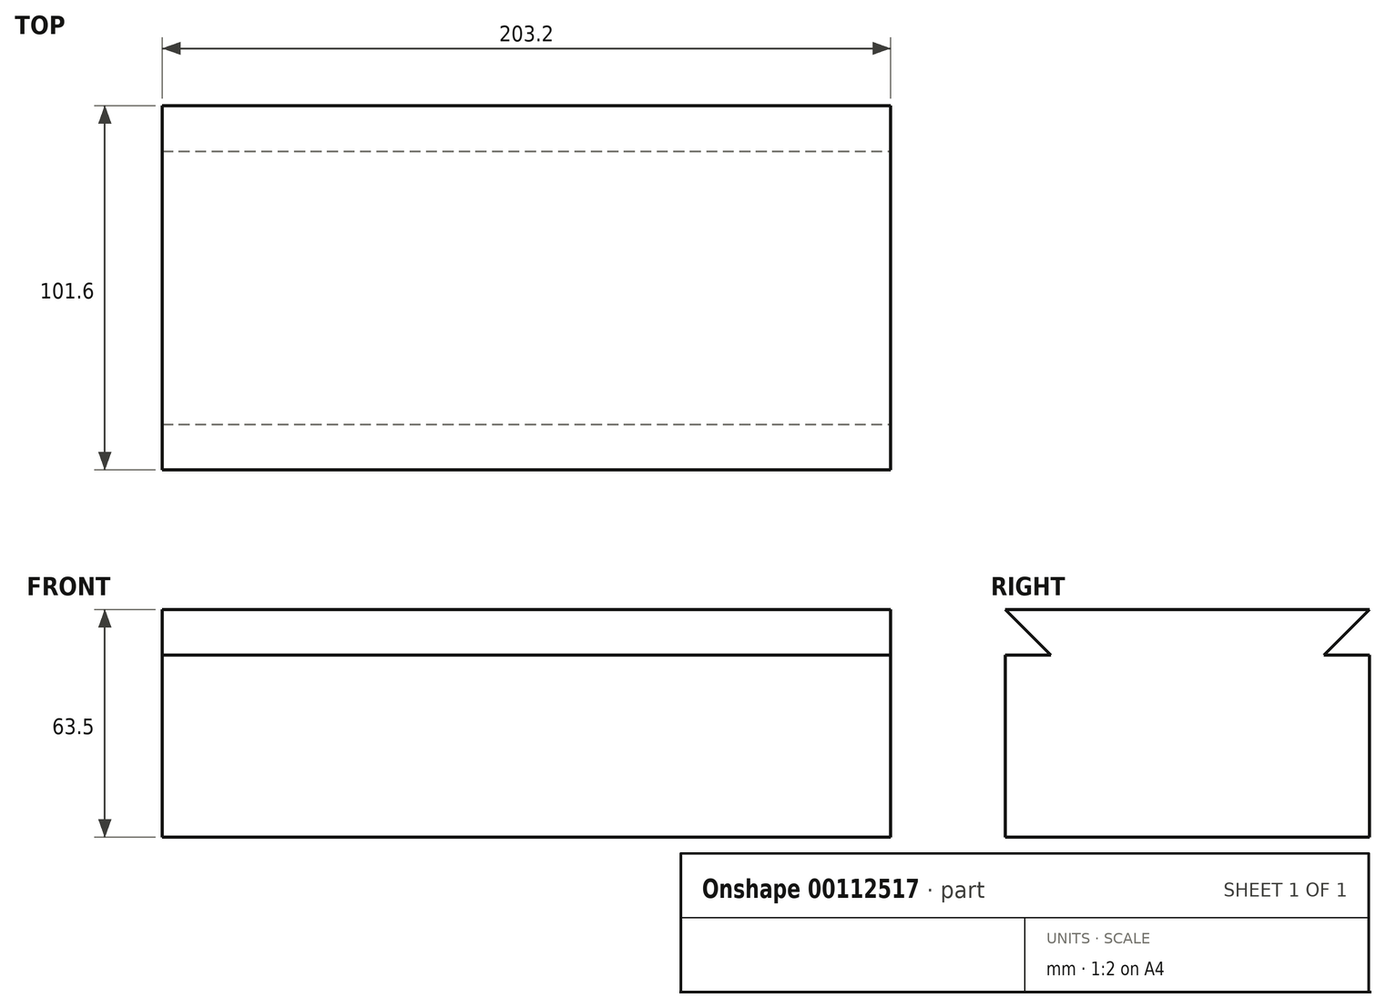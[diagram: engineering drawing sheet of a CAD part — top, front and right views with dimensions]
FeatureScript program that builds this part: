
annotation { "Feature Type Name" : "Feature", "Feature Type Description" : "" }
export const myFeature = defineFeature(function(context is Context, id is Id, definition is map)
    precondition{}
    {
        {
            var Q0;
            Q0=qCreatedBy(makeId("Top.planeOp"),FACE);
            var sketch = newSketch(context, id + "F0", { "sketchPlane" : qUnion([Q0])});
            skLineSegment(sketch, "E0.bottom", {"start": v(101.6, -50.8) * mm, "end": v(-101.6, -50.8) * mm});
            skLineSegment(sketch, "E0.top", {"start": v(101.6, 50.8) * mm, "end": v(-101.6, 50.8) * mm});
            skLineSegment(sketch, "E0.left", {"start": v(101.6, -50.8) * mm, "end": v(101.6, 50.8) * mm});
            skLineSegment(sketch, "E0.right", {"start": v(-101.6, -50.8) * mm, "end": v(-101.6, 50.8) * mm});
            skPoint(sketch, "E0.middle", {"position": v(0, 0) * mm});
            skSolve(sketch);
        }
        {
            var Q0;
            Q0=makeQuery(id+"F0.imprint","IMPRINT",FACE,{"disambiguationData":[TD([[makeQuery(id+"F0.imprint","IMPRINT",EDGE,{"derivedFrom":sQuery(id+"F0.wireOp",EDGE,"E0.bottom")}),-1.0]])]});
            extrude(context, id + "F1", {"entities" : qUnion([Q0]), "depth" : 63.5 * mm});
        }
        {
            var Q0;
            Q0=makeQuery(id+"F1.opExtrude","SWEPT_FACE",FACE,{"disambiguationData":[OSD([sQuery(id+"F0.wireOp",EDGE,"E0.left")])]});
            var sketch = newSketch(context, id + "F2", { "sketchPlane" : qUnion([Q0])});
            skLineSegment(sketch, "E1", {"start": v(-50.8, 63.5) * mm, "end": v(-50.8, 50.8) * mm});
            skLineSegment(sketch, "E2", {"start": v(-50.8, 50.8) * mm, "end": v(-38.1, 50.8) * mm});
            skLineSegment(sketch, "E3", {"start": v(-38.1, 50.8) * mm, "end": v(-50.8, 63.5) * mm});
            skLineSegment(sketch, "E4", {"start": v(50.8, 63.5) * mm, "end": v(50.8, 50.8) * mm});
            skLineSegment(sketch, "E5", {"start": v(50.8, 50.8) * mm, "end": v(38.1, 50.8) * mm});
            skLineSegment(sketch, "E6", {"start": v(38.1, 50.8) * mm, "end": v(50.8, 63.5) * mm});
            skSolve(sketch);
        }
        {
            var Q0;
            Q0=makeQuery(id+"F2.imprint","IMPRINT",FACE,{"disambiguationData":[TD([[makeQuery(id+"F2.imprint","IMPRINT",EDGE,{"derivedFrom":sQuery(id+"F2.wireOp",EDGE,"E4")}),-1.0]])]});
            extrude(context, id + "F3", {"entities" : qUnion([Q0]), "operationType" : NewBodyOperationType.REMOVE, "oppositeDirection" : true, "depth" : 215.9 * mm});
        }
        {
            var Q0;
            Q0=makeQuery(id+"F1.opExtrude","SWEPT_FACE",FACE,{"disambiguationData":[OSD([sQuery(id+"F0.wireOp",EDGE,"E0.left")])]});
            var sketch = newSketch(context, id + "F4", { "sketchPlane" : qUnion([Q0])});
            skLineSegment(sketch, "E7", {"start": v(-50.8, 63.5) * mm, "end": v(-50.8, 50.8) * mm});
            skLineSegment(sketch, "E8", {"start": v(-50.8, 50.8) * mm, "end": v(-38.1, 50.8) * mm});
            skLineSegment(sketch, "E9", {"start": v(-38.1, 50.8) * mm, "end": v(-50.8, 63.5) * mm});
            skSolve(sketch);
        }
        {
            var Q0;
            Q0=makeQuery(id+"F4.imprint","IMPRINT",FACE,{"disambiguationData":[TD([[makeQuery(id+"F4.imprint","IMPRINT",EDGE,{"derivedFrom":sQuery(id+"F4.wireOp",EDGE,"E7")}),1.0]])]});
            extrude(context, id + "F5", {"entities" : qUnion([Q0]), "operationType" : NewBodyOperationType.REMOVE, "oppositeDirection" : true, "depth" : 215.9 * mm});
        }
    });
